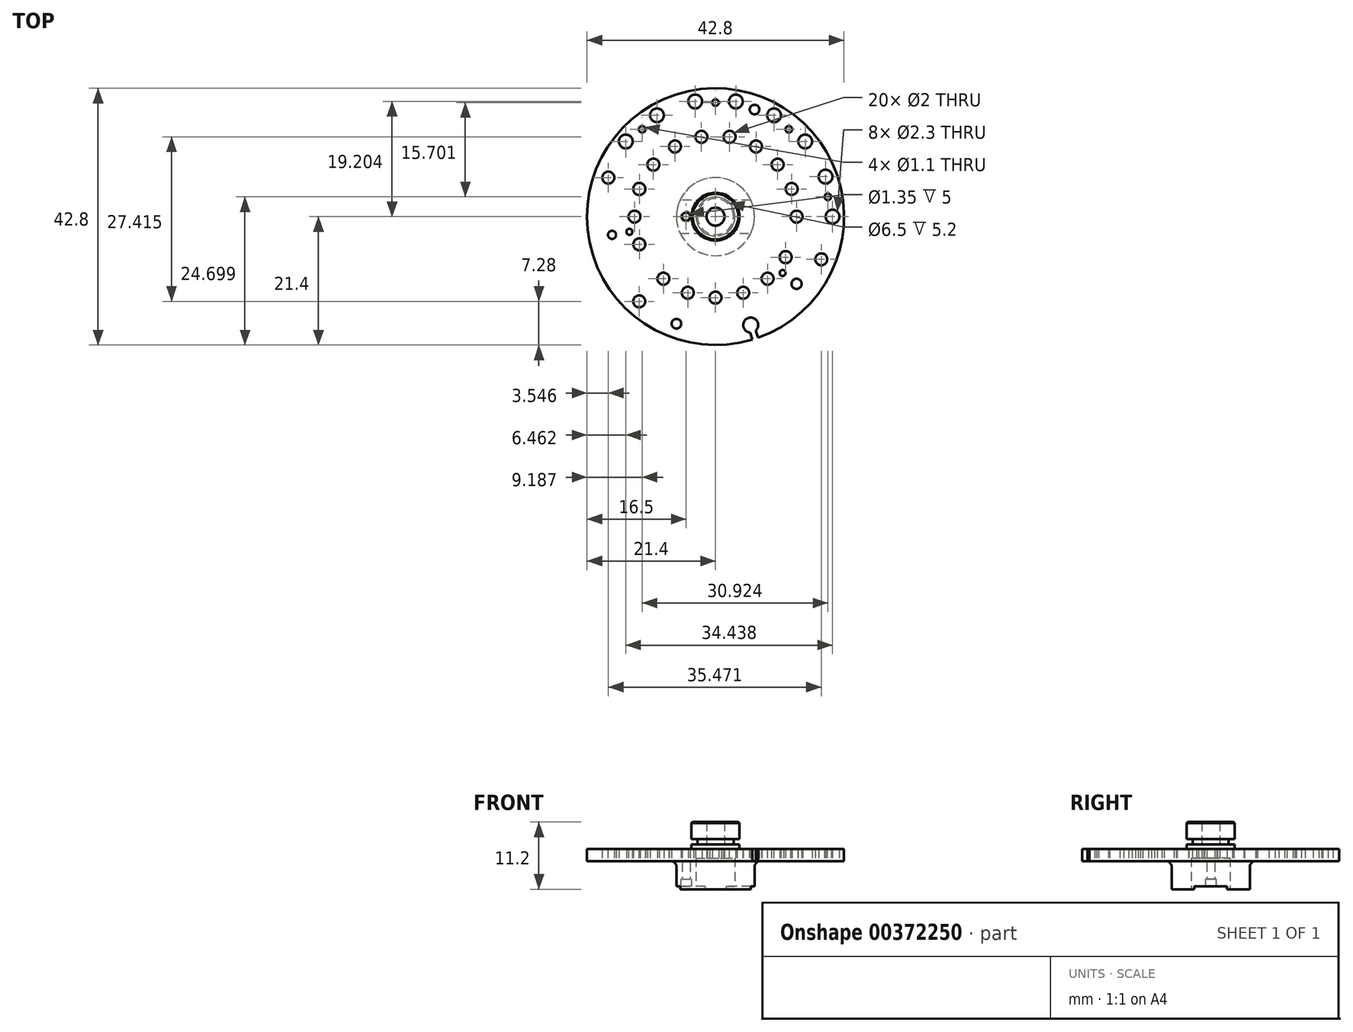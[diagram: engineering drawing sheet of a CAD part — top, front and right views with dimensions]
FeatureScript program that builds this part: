
annotation { "Feature Type Name" : "Feature", "Feature Type Description" : "" }
export const myFeature = defineFeature(function(context is Context, id is Id, definition is map)
    precondition{}
    {
        {
            var Q0;
            Q0=qCreatedBy(makeId("Front.planeOp"),FACE);
            var sketch = newSketch(context, id + "F0", { "sketchPlane" : qUnion([Q0])});
            skLineSegment(sketch, "E0", {"start": v(3.25, 0) * mm, "end": v(6.5, 0) * mm});
            skLineSegment(sketch, "E1", {"start": v(6.5, 0) * mm, "end": v(6.5, 4.7) * mm});
            skLineSegment(sketch, "E2", {"start": v(6.5, 4.7) * mm, "end": v(21.4, 4.7) * mm});
            skLineSegment(sketch, "E3", {"start": v(21.4, 4.7) * mm, "end": v(21.4, 6.7) * mm});
            skLineSegment(sketch, "E4", {"start": v(21.4, 6.7) * mm, "end": v(4, 6.7) * mm});
            skLineSegment(sketch, "E5", {"start": v(4, 6.7) * mm, "end": v(4, 7.5) * mm});
            skLineSegment(sketch, "E6", {"start": v(4, 11.2) * mm, "end": v(1.5, 11.2) * mm});
            skLineSegment(sketch, "E7", {"start": v(1.5, 11.2) * mm, "end": v(1.5, 5.2) * mm});
            skLineSegment(sketch, "E8", {"start": v(1.5, 5.2) * mm, "end": v(3.25, 5.2) * mm});
            skLineSegment(sketch, "E9", {"start": v(3.25, 5.2) * mm, "end": v(3.25, 0) * mm});
            skLineSegment(sketch, "E10", {"start": v(4, 7.5) * mm, "end": v(3, 7.5) * mm});
            skLineSegment(sketch, "E11", {"start": v(3, 7.5) * mm, "end": v(3, 8.35) * mm});
            skLineSegment(sketch, "E12", {"start": v(3, 8.35) * mm, "end": v(4, 8.35) * mm});
            skLineSegment(sketch, "E13", {"start": v(4, 8.35) * mm, "end": v(4, 11.2) * mm});
            skLineSegment(sketch, "E14", {"start": v(0, 0) * mm, "end": v(0, 11.2) * mm, "construction": true});
            skSolve(sketch);
        }
        {
            var Q0;
            Q0=makeQuery(id+"F0.imprint","IMPRINT",FACE,{"disambiguationData":[TD([[makeQuery(id+"F0.imprint","IMPRINT",EDGE,{"derivedFrom":sQuery(id+"F0.wireOp",EDGE,"E0")}),1.0]])]});
            var Q1;
            Q1=sQuery(id+"F0.wireOp",EDGE,"E14");
            revolve(context, id + "F1", {"entities" : qUnion([Q0]), "axis" : qUnion([Q1]), "revolveType" : RevolveType.FULL});
        }
        {
            var Q0;
            Q0=makeQuery(id+"F1.opRevolve","SWEPT_FACE",FACE,{"disambiguationData":[OSD([sQuery(id+"F0.wireOp",EDGE,"E2")])]});
            var sketch = newSketch(context, id + "F2", { "sketchPlane" : qUnion([Q0])});
            skLineSegment(sketch, "E15", {"start": v(21.4, 0) * mm, "end": v(0, 0) * mm, "construction": true});
            skLineSegment(sketch, "E16", {"start": v(0, 0) * mm, "end": v(20.1, -7.32) * mm, "construction": true});
            skLineSegment(sketch, "E17", {"start": v(0, 0) * mm, "end": v(16.4, -13.76) * mm, "construction": true});
            skLineSegment(sketch, "E18", {"start": v(0, 0) * mm, "end": v(10.7, -18.53) * mm, "construction": true});
            skLineSegment(sketch, "E19", {"start": v(0, 0) * mm, "end": v(3.72, -21.07) * mm, "construction": true});
            skLineSegment(sketch, "E20", {"start": v(0, 0) * mm, "end": v(-3.72, -21.07) * mm, "construction": true});
            skLineSegment(sketch, "E21", {"start": v(0, 0) * mm, "end": v(-10.7, -18.53) * mm, "construction": true});
            skLineSegment(sketch, "E22", {"start": v(0, 0) * mm, "end": v(-16.4, -13.76) * mm, "construction": true});
            skLineSegment(sketch, "E23", {"start": v(0, 0) * mm, "end": v(-20.1, -7.32) * mm, "construction": true});
            skLineSegment(sketch, "E24", {"start": v(0, 0) * mm, "end": v(-21.4, 0) * mm, "construction": true});
            skLineSegment(sketch, "E25", {"start": v(0, 0) * mm, "end": v(-20.1, 7.32) * mm, "construction": true});
            skLineSegment(sketch, "E26", {"start": v(0, 0) * mm, "end": v(18.53, 10.7) * mm, "construction": true});
            skLineSegment(sketch, "E27", {"start": v(0, 0) * mm, "end": v(13.76, 16.4) * mm, "construction": true});
            skLineSegment(sketch, "E28", {"start": v(0, 0) * mm, "end": v(7.32, 20.1) * mm, "construction": true});
            skLineSegment(sketch, "E29", {"start": v(0, 0) * mm, "end": v(0, 21.4) * mm, "construction": true});
            skLineSegment(sketch, "E30", {"start": v(0, 0) * mm, "end": v(-7.32, 20.1) * mm, "construction": true});
            skLineSegment(sketch, "E31", {"start": v(0, 0) * mm, "end": v(-13.76, 16.4) * mm, "construction": true});
            skCircle(sketch, "E32", {"center": v(0, 0) * mm, "radius": 19.5 * mm, "construction": true});
            skCircle(sketch, "E33", {"center": v(0, 0) * mm, "radius": 13.5 * mm, "construction": true});
            skCircle(sketch, "E34", {"center": v(19.5, 0) * mm, "radius": 1.15 * mm});
            skCircle(sketch, "E35", {"center": v(18.32, -6.67) * mm, "radius": 1.15 * mm});
            skCircle(sketch, "E36", {"center": v(14.94, -12.53) * mm, "radius": 1.15 * mm});
            skCircle(sketch, "E37", {"center": v(9.75, -16.89) * mm, "radius": 1.15 * mm});
            skCircle(sketch, "E38", {"center": v(3.39, -19.2) * mm, "radius": 1.15 * mm});
            skCircle(sketch, "E39", {"center": v(-3.39, -19.2) * mm, "radius": 1.15 * mm});
            skCircle(sketch, "E40", {"center": v(-9.75, -16.89) * mm, "radius": 1.15 * mm});
            skCircle(sketch, "E41", {"center": v(-14.94, -12.53) * mm, "radius": 1.15 * mm});
            skCircle(sketch, "E42", {"center": v(-17.85, -6.5) * mm, "radius": 1 * mm});
            skCircle(sketch, "E43", {"center": v(11.7, 6.75) * mm, "radius": 1 * mm});
            skCircle(sketch, "E44", {"center": v(8.68, 10.34) * mm, "radius": 1 * mm});
            skCircle(sketch, "E45", {"center": v(12.69, -4.62) * mm, "radius": 1 * mm});
            skCircle(sketch, "E46", {"center": v(13.5, 0) * mm, "radius": 1 * mm});
            skCircle(sketch, "E47", {"center": v(10.34, -8.68) * mm, "radius": 1 * mm});
            skCircle(sketch, "E48", {"center": v(6.75, -11.7) * mm, "radius": 1 * mm});
            skCircle(sketch, "E49", {"center": v(2.34, -13.3) * mm, "radius": 1 * mm});
            skCircle(sketch, "E50", {"center": v(-2.34, -13.3) * mm, "radius": 1 * mm});
            skCircle(sketch, "E51", {"center": v(-6.75, -11.7) * mm, "radius": 1 * mm});
            skCircle(sketch, "E52", {"center": v(-10.34, -8.68) * mm, "radius": 1 * mm});
            skCircle(sketch, "E53", {"center": v(-12.69, -4.62) * mm, "radius": 1 * mm});
            skCircle(sketch, "E54", {"center": v(-13.5, 0) * mm, "radius": 1 * mm});
            skCircle(sketch, "E55", {"center": v(-12.69, 4.62) * mm, "radius": 1 * mm});
            skCircle(sketch, "E56", {"center": v(-8.68, 10.34) * mm, "radius": 1 * mm});
            skCircle(sketch, "E57", {"center": v(-4.62, 12.69) * mm, "radius": 1 * mm});
            skCircle(sketch, "E58", {"center": v(0, 13.5) * mm, "radius": 1 * mm});
            skCircle(sketch, "E59", {"center": v(4.62, 12.69) * mm, "radius": 1 * mm});
            skLineSegment(sketch, "E60", {"start": v(0, 0) * mm, "end": v(21.07, -3.72) * mm, "construction": true});
            skLineSegment(sketch, "E61", {"start": v(0, 0) * mm, "end": v(13.76, -16.4) * mm, "construction": true});
            skLineSegment(sketch, "E62", {"start": v(0, 0) * mm, "end": v(7.32, -20.1) * mm, "construction": true});
            skLineSegment(sketch, "E63", {"start": v(0, 0) * mm, "end": v(0, -21.4) * mm, "construction": true});
            skLineSegment(sketch, "E64", {"start": v(0, 0) * mm, "end": v(-13.76, -16.4) * mm, "construction": true});
            skCircle(sketch, "E65", {"center": v(18.71, -3.3) * mm, "radius": 0.55 * mm});
            skCircle(sketch, "E66", {"center": v(12.21, -14.55) * mm, "radius": 0.55 * mm});
            skCircle(sketch, "E67", {"center": v(0, -19) * mm, "radius": 0.55 * mm});
            skCircle(sketch, "E68", {"center": v(-12.21, -14.55) * mm, "radius": 0.55 * mm});
            skCircle(sketch, "E69", {"center": v(6.5, -17.85) * mm, "radius": 0.8 * mm});
            skCircle(sketch, "E70", {"center": v(0, 0) * mm, "radius": 19 * mm, "construction": true});
            skLineSegment(sketch, "E71", {"start": v(0, 0) * mm, "end": v(17.62, 7.12) * mm, "construction": true});
            skCircle(sketch, "E72", {"center": v(17.62, 7.12) * mm, "radius": 1 * mm});
            skLineSegment(sketch, "E73", {"start": v(0, 0) * mm, "end": v(5.87, 18.07) * mm, "construction": true});
            skArc(sketch, "E74", {"start": v(5.75, 19.31) * mm, "mid": v(5.49, 16.88) * mm, "end": v(6.7, 19) * mm});
            skLineSegment(sketch, "E75", {"start": v(5.75, 19.31) * mm, "end": v(6.14, 20.5) * mm});
            skLineSegment(sketch, "E76", {"start": v(6.7, 19) * mm, "end": v(7.09, 20.2) * mm});
            skCircle(sketch, "E77", {"center": v(13.5, 11.2) * mm, "radius": 0.85 * mm});
            skCircle(sketch, "E78", {"center": v(11.18, 9.38) * mm, "radius": 0.5 * mm});
            skLineSegment(sketch, "E79", {"start": v(11.18, 9.38) * mm, "end": v(0, 0) * mm, "construction": true});
            skCircle(sketch, "E80", {"center": v(-6.5, 17.85) * mm, "radius": 0.8 * mm});
            skCircle(sketch, "E81", {"center": v(-12.71, 14.12) * mm, "radius": 1 * mm});
            skLineSegment(sketch, "E82", {"start": v(0, 0) * mm, "end": v(-12.71, 14.12) * mm, "construction": true});
            skLineSegment(sketch, "E83", {"start": v(0, 0) * mm, "end": v(-17.23, 3.04) * mm, "construction": true});
            skPoint(sketch, "E84", {"position": v(-14.33, 2.53) * mm});
            skCircle(sketch, "E85", {"center": v(-17.23, 3.04) * mm, "radius": 0.68 * mm});
            skCircle(sketch, "E86", {"center": v(-14.33, 2.53) * mm, "radius": 0.5 * mm});
            skSolve(sketch);
        }
        {
            var Q0;
            {Q0=qUnion([makeQuery(id+"F2.imprint","IMPRINT",FACE,{"disambiguationData":[TD([[makeQuery(id+"F2.imprint","IMPRINT",EDGE,{"derivedFrom":sQuery(id+"F2.wireOp",EDGE,"E34")}),1.0]])]}),makeQuery(id+"F2.imprint","IMPRINT",FACE,{"disambiguationData":[TD([[makeQuery(id+"F2.imprint","IMPRINT",EDGE,{"derivedFrom":sQuery(id+"F2.wireOp",EDGE,"E35")}),1.0]])]}),makeQuery(id+"F2.imprint","IMPRINT",FACE,{"disambiguationData":[TD([[makeQuery(id+"F2.imprint","IMPRINT",EDGE,{"derivedFrom":sQuery(id+"F2.wireOp",EDGE,"E36")}),1.0]])]}),makeQuery(id+"F2.imprint","IMPRINT",FACE,{"disambiguationData":[TD([[makeQuery(id+"F2.imprint","IMPRINT",EDGE,{"derivedFrom":sQuery(id+"F2.wireOp",EDGE,"E37")}),1.0]])]}),makeQuery(id+"F2.imprint","IMPRINT",FACE,{"disambiguationData":[TD([[makeQuery(id+"F2.imprint","IMPRINT",EDGE,{"derivedFrom":sQuery(id+"F2.wireOp",EDGE,"E38")}),1.0]])]}),makeQuery(id+"F2.imprint","IMPRINT",FACE,{"disambiguationData":[TD([[makeQuery(id+"F2.imprint","IMPRINT",EDGE,{"derivedFrom":sQuery(id+"F2.wireOp",EDGE,"E39")}),1.0]])]}),makeQuery(id+"F2.imprint","IMPRINT",FACE,{"disambiguationData":[TD([[makeQuery(id+"F2.imprint","IMPRINT",EDGE,{"derivedFrom":sQuery(id+"F2.wireOp",EDGE,"E40")}),1.0]])]}),makeQuery(id+"F2.imprint","IMPRINT",FACE,{"disambiguationData":[TD([[makeQuery(id+"F2.imprint","IMPRINT",EDGE,{"derivedFrom":sQuery(id+"F2.wireOp",EDGE,"E41")}),1.0]])]}),makeQuery(id+"F2.imprint","IMPRINT",FACE,{"disambiguationData":[TD([[makeQuery(id+"F2.imprint","IMPRINT",EDGE,{"derivedFrom":sQuery(id+"F2.wireOp",EDGE,"E42")}),1.0]])]}),makeQuery(id+"F2.imprint","IMPRINT",FACE,{"disambiguationData":[TD([[makeQuery(id+"F2.imprint","IMPRINT",EDGE,{"derivedFrom":sQuery(id+"F2.wireOp",EDGE,"E43")}),1.0]])]}),makeQuery(id+"F2.imprint","IMPRINT",FACE,{"disambiguationData":[TD([[makeQuery(id+"F2.imprint","IMPRINT",EDGE,{"derivedFrom":sQuery(id+"F2.wireOp",EDGE,"E44")}),1.0]])]}),makeQuery(id+"F2.imprint","IMPRINT",FACE,{"disambiguationData":[TD([[makeQuery(id+"F2.imprint","IMPRINT",EDGE,{"derivedFrom":sQuery(id+"F2.wireOp",EDGE,"E45")}),1.0]])]}),makeQuery(id+"F2.imprint","IMPRINT",FACE,{"disambiguationData":[TD([[makeQuery(id+"F2.imprint","IMPRINT",EDGE,{"derivedFrom":sQuery(id+"F2.wireOp",EDGE,"E46")}),1.0]])]}),makeQuery(id+"F2.imprint","IMPRINT",FACE,{"disambiguationData":[TD([[makeQuery(id+"F2.imprint","IMPRINT",EDGE,{"derivedFrom":sQuery(id+"F2.wireOp",EDGE,"E47")}),1.0]])]}),makeQuery(id+"F2.imprint","IMPRINT",FACE,{"disambiguationData":[TD([[makeQuery(id+"F2.imprint","IMPRINT",EDGE,{"derivedFrom":sQuery(id+"F2.wireOp",EDGE,"E48")}),1.0]])]}),makeQuery(id+"F2.imprint","IMPRINT",FACE,{"disambiguationData":[TD([[makeQuery(id+"F2.imprint","IMPRINT",EDGE,{"derivedFrom":sQuery(id+"F2.wireOp",EDGE,"E49")}),1.0]])]}),makeQuery(id+"F2.imprint","IMPRINT",FACE,{"disambiguationData":[TD([[makeQuery(id+"F2.imprint","IMPRINT",EDGE,{"derivedFrom":sQuery(id+"F2.wireOp",EDGE,"E50")}),1.0]])]}),makeQuery(id+"F2.imprint","IMPRINT",FACE,{"disambiguationData":[TD([[makeQuery(id+"F2.imprint","IMPRINT",EDGE,{"derivedFrom":sQuery(id+"F2.wireOp",EDGE,"E51")}),1.0]])]}),makeQuery(id+"F2.imprint","IMPRINT",FACE,{"disambiguationData":[TD([[makeQuery(id+"F2.imprint","IMPRINT",EDGE,{"derivedFrom":sQuery(id+"F2.wireOp",EDGE,"E52")}),1.0]])]}),makeQuery(id+"F2.imprint","IMPRINT",FACE,{"disambiguationData":[TD([[makeQuery(id+"F2.imprint","IMPRINT",EDGE,{"derivedFrom":sQuery(id+"F2.wireOp",EDGE,"E53")}),1.0]])]}),makeQuery(id+"F2.imprint","IMPRINT",FACE,{"disambiguationData":[TD([[makeQuery(id+"F2.imprint","IMPRINT",EDGE,{"derivedFrom":sQuery(id+"F2.wireOp",EDGE,"E54")}),1.0]])]}),makeQuery(id+"F2.imprint","IMPRINT",FACE,{"disambiguationData":[TD([[makeQuery(id+"F2.imprint","IMPRINT",EDGE,{"derivedFrom":sQuery(id+"F2.wireOp",EDGE,"E55")}),1.0]])]}),makeQuery(id+"F2.imprint","IMPRINT",FACE,{"disambiguationData":[TD([[makeQuery(id+"F2.imprint","IMPRINT",EDGE,{"derivedFrom":sQuery(id+"F2.wireOp",EDGE,"E56")}),1.0]])]}),makeQuery(id+"F2.imprint","IMPRINT",FACE,{"disambiguationData":[TD([[makeQuery(id+"F2.imprint","IMPRINT",EDGE,{"derivedFrom":sQuery(id+"F2.wireOp",EDGE,"E57")}),1.0]])]}),makeQuery(id+"F2.imprint","IMPRINT",FACE,{"disambiguationData":[TD([[makeQuery(id+"F2.imprint","IMPRINT",EDGE,{"derivedFrom":sQuery(id+"F2.wireOp",EDGE,"E58")}),1.0]])]}),makeQuery(id+"F2.imprint","IMPRINT",FACE,{"disambiguationData":[TD([[makeQuery(id+"F2.imprint","IMPRINT",EDGE,{"derivedFrom":sQuery(id+"F2.wireOp",EDGE,"E59")}),1.0]])]}),makeQuery(id+"F2.imprint","IMPRINT",FACE,{"disambiguationData":[TD([[makeQuery(id+"F2.imprint","IMPRINT",EDGE,{"derivedFrom":sQuery(id+"F2.wireOp",EDGE,"E65")}),1.0]])]}),makeQuery(id+"F2.imprint","IMPRINT",FACE,{"disambiguationData":[TD([[makeQuery(id+"F2.imprint","IMPRINT",EDGE,{"derivedFrom":sQuery(id+"F2.wireOp",EDGE,"E66")}),1.0]])]}),makeQuery(id+"F2.imprint","IMPRINT",FACE,{"disambiguationData":[TD([[makeQuery(id+"F2.imprint","IMPRINT",EDGE,{"derivedFrom":sQuery(id+"F2.wireOp",EDGE,"E67")}),1.0]])]}),makeQuery(id+"F2.imprint","IMPRINT",FACE,{"disambiguationData":[TD([[makeQuery(id+"F2.imprint","IMPRINT",EDGE,{"derivedFrom":sQuery(id+"F2.wireOp",EDGE,"E68")}),1.0]])]}),makeQuery(id+"F2.imprint","IMPRINT",FACE,{"disambiguationData":[TD([[makeQuery(id+"F2.imprint","IMPRINT",EDGE,{"derivedFrom":sQuery(id+"F2.wireOp",EDGE,"E69")}),1.0]])]}),makeQuery(id+"F2.imprint","IMPRINT",FACE,{"disambiguationData":[TD([[makeQuery(id+"F2.imprint","IMPRINT",EDGE,{"derivedFrom":sQuery(id+"F2.wireOp",EDGE,"E72")}),1.0]])]}),makeQuery(id+"F2.imprint","IMPRINT",FACE,{"disambiguationData":[TD([[makeQuery(id+"F2.imprint","IMPRINT",EDGE,{"derivedFrom":sQuery(id+"F2.wireOp",EDGE,"E77")}),1.0]])]}),makeQuery(id+"F2.imprint","IMPRINT",FACE,{"disambiguationData":[TD([[makeQuery(id+"F2.imprint","IMPRINT",EDGE,{"derivedFrom":sQuery(id+"F2.wireOp",EDGE,"E78")}),1.0]])]}),makeQuery(id+"F2.imprint","IMPRINT",FACE,{"disambiguationData":[TD([[makeQuery(id+"F2.imprint","IMPRINT",EDGE,{"derivedFrom":sQuery(id+"F2.wireOp",EDGE,"E80")}),1.0]])]}),makeQuery(id+"F2.imprint","IMPRINT",FACE,{"disambiguationData":[TD([[makeQuery(id+"F2.imprint","IMPRINT",EDGE,{"derivedFrom":sQuery(id+"F2.wireOp",EDGE,"E81")}),1.0]])]}),makeQuery(id+"F2.imprint","IMPRINT",FACE,{"disambiguationData":[TD([[makeQuery(id+"F2.imprint","IMPRINT",EDGE,{"derivedFrom":sQuery(id+"F2.wireOp",EDGE,"E85")}),1.0]])]}),makeQuery(id+"F2.imprint","IMPRINT",FACE,{"disambiguationData":[TD([[makeQuery(id+"F2.imprint","IMPRINT",EDGE,{"derivedFrom":sQuery(id+"F2.wireOp",EDGE,"E86")}),1.0]])]})]);}
            var Q1;
            Q1=makeQuery(id+"F2.imprint","IMPRINT",FACE,{"disambiguationData":[TD([[makeQuery(id+"F2.imprint","IMPRINT",EDGE,{"derivedFrom":sQuery(id+"F2.wireOp",EDGE,"E74")}),1.0]])]});
            extrude(context, id + "F3", {"entities" : qUnion([Q0, Q1]), "operationType" : NewBodyOperationType.REMOVE, "endBound" : BoundingType.THROUGH_ALL, "oppositeDirection" : true, "depth" : 25 * mm});
        }
        {
            var Q0;
            Q0=makeQuery(id+"F1.opRevolve","SWEPT_EDGE",EDGE,{"disambiguationData":[OSD([sQuery(id+"F0.wireOp",EDGE,"E1"),sQuery(id+"F0.wireOp",EDGE,"E2")])]});
            fillet(context, id + "F4", {"entities" : qUnion([Q0]), "radius" : 1 * mm, "tangentPropagation" : true, "allowEdgeOverflow" : false});
        }
        {
            var Q0;
            Q0=makeQuery(id+"F1.opRevolve","SWEPT_EDGE",EDGE,{"disambiguationData":[OSD([sQuery(id+"F0.wireOp",EDGE,"E4"),sQuery(id+"F0.wireOp",EDGE,"E5")])]});
            fillet(context, id + "F5", {"entities" : qUnion([Q0]), "radius" : 0.2 * mm, "tangentPropagation" : true, "allowEdgeOverflow" : false});
        }
        {
            var Q0;
            Q0=makeQuery(id+"F1.opRevolve","SWEPT_EDGE",EDGE,{"disambiguationData":[OSD([sQuery(id+"F0.wireOp",EDGE,"E6"),sQuery(id+"F0.wireOp",EDGE,"E13")])]});
            chamfer(context, id + "F6", {"entities" : qUnion([Q0]), "width" : 0.2 * mm, "tangentPropagation" : true});
        }
        {
            var Q0;
            Q0=makeQuery(id+"F1.opRevolve","SWEPT_FACE",FACE,{"disambiguationData":[OSD([sQuery(id+"F0.wireOp",EDGE,"E0")])]});
            var sketch = newSketch(context, id + "F7", { "sketchPlane" : qUnion([Q0])});
            skLineSegment(sketch, "E87", {"start": v(5.89, -2.75) * mm, "end": v(-5.89, -2.75) * mm});
            skLineSegment(sketch, "E88", {"start": v(-5.89, 2.75) * mm, "end": v(5.89, 2.75) * mm});
            skSolve(sketch);
        }
        {
            var Q0;
            {var subQ0=sQuery(id+"F0.wireOp",EDGE,"E0");var subQ4=sQuery(id+"F7.wireOp",EDGE,"E87");var subQ6=makeQuery(id+"F1.opRevolve","SWEPT_EDGE",EDGE,{"disambiguationData":[OSD([subQ0,sQuery(id+"F0.wireOp",EDGE,"E1")])]});var subQ8=makeQuery(id+"F7.imprint","INTERSECT",VERTEX,{"disambiguationData":[OD(0.0)],"derivedFrom":[subQ6,subQ4]});Q0=makeQuery(id+"F7.imprint","IMPRINT",FACE,{"disambiguationData":[TD([[makeQuery(id+"F7.imprint","IMPRINT",EDGE,{"disambiguationData":[TD([[subQ8,-1.0]])],"derivedFrom":subQ4}),-1.0]])]});}
            var Q1;
            {var subQ0=sQuery(id+"F0.wireOp",EDGE,"E0");var subQ4=sQuery(id+"F7.wireOp",EDGE,"E87");var subQ6=makeQuery(id+"F1.opRevolve","SWEPT_EDGE",EDGE,{"disambiguationData":[OSD([subQ0,sQuery(id+"F0.wireOp",EDGE,"E1")])]});var subQ8=makeQuery(id+"F7.imprint","INTERSECT",VERTEX,{"disambiguationData":[OD(1.0)],"derivedFrom":[subQ6,subQ4]});Q1=makeQuery(id+"F7.imprint","IMPRINT",FACE,{"disambiguationData":[TD([[makeQuery(id+"F7.imprint","IMPRINT",EDGE,{"disambiguationData":[TD([[subQ8,1.0]])],"derivedFrom":subQ4}),-1.0]])]});}
            extrude(context, id + "F8", {"entities" : qUnion([Q0, Q1]), "operationType" : NewBodyOperationType.REMOVE, "oppositeDirection" : true, "depth" : 0.5 * mm});
        }
        {
            var Q0;
            {var subQ0=sQuery(id+"F0.wireOp",EDGE,"E0");var subQ1=sQuery(id+"F0.wireOp",EDGE,"E1");var subQ2=sQuery(id+"F0.wireOp",EDGE,"E9");var subQ3=sQuery(id+"F7.wireOp",EDGE,"E87");var subQ4=sQuery(id+"F7.wireOp",EDGE,"E88");var subQ5=makeQuery(id+"F1.opRevolve","SWEPT_EDGE",EDGE,{"disambiguationData":[OSD([subQ0,subQ2])]});var subQ6=makeQuery(id+"F7.imprint","INTERSECT",VERTEX,{"disambiguationData":[OD(1.0)],"derivedFrom":[subQ5,subQ3]});var subQ7=makeQuery(id+"F1.opRevolve","SWEPT_EDGE",EDGE,{"disambiguationData":[OSD([subQ0,subQ1])]});var subQ8=makeQuery(id+"F7.imprint","INTERSECT",VERTEX,{"disambiguationData":[OD(1.0)],"derivedFrom":[subQ7,subQ3]});var subQ10=makeQuery(id+"F7.imprint","INTERSECT",VERTEX,{"disambiguationData":[OD(0.0)],"derivedFrom":[subQ7,subQ4]});Q0=makeQuery(id+"F8.boolean.opBoolean","COPY",FACE,{"derivedFrom":makeQuery(id+"F8.opExtrude","CAP_FACE",FACE,{"disambiguationData":[OSD([subQ0,subQ1,subQ2,subQ3,subQ4]),TDD([makeQuery(id+"F7.imprint","IMPRINT",EDGE,{"disambiguationData":[TD([[subQ8,1.0]])],"derivedFrom":subQ3}),makeQuery(id+"F7.imprint","IMPRINT",EDGE,{"disambiguationData":[TD([[subQ10,-1.0]])],"derivedFrom":subQ4}),makeQuery(id+"F7.imprint","IMPRINT",EDGE,{"disambiguationData":[TD([[subQ8,1.0]])],"derivedFrom":subQ7}),makeQuery(id+"F7.imprint","IMPRINT",EDGE,{"disambiguationData":[TD([[subQ6,1.0]])],"derivedFrom":subQ5})])],"isStart":false})});}
            var sketch = newSketch(context, id + "F9", { "sketchPlane" : qUnion([Q0])});
            skCircle(sketch, "E89", {"center": v(-4.9, 0) * mm, "radius": 0.68 * mm});
            skSolve(sketch);
        }
        {
            var Q0;
            Q0=makeQuery(id+"F9.imprint","IMPRINT",FACE,{"disambiguationData":[TD([[makeQuery(id+"F9.imprint","IMPRINT",EDGE,{"derivedFrom":sQuery(id+"F9.wireOp",EDGE,"E89")}),1.0]])]});
            extrude(context, id + "F10", {"entities" : qUnion([Q0]), "operationType" : NewBodyOperationType.REMOVE, "endBound" : BoundingType.THROUGH_ALL, "oppositeDirection" : true, "depth" : 25 * mm});
        }
        {
            var Q0;
            {var subQ0=sQuery(id+"F0.wireOp",EDGE,"E0");var subQ1=sQuery(id+"F0.wireOp",EDGE,"E1");var subQ2=sQuery(id+"F0.wireOp",EDGE,"E9");var subQ3=sQuery(id+"F7.wireOp",EDGE,"E87");var subQ4=sQuery(id+"F7.wireOp",EDGE,"E88");var subQ5=makeQuery(id+"F1.opRevolve","SWEPT_EDGE",EDGE,{"disambiguationData":[OSD([subQ0,subQ2])]});var subQ6=makeQuery(id+"F7.imprint","INTERSECT",VERTEX,{"disambiguationData":[OD(1.0)],"derivedFrom":[subQ5,subQ3]});var subQ7=makeQuery(id+"F1.opRevolve","SWEPT_EDGE",EDGE,{"disambiguationData":[OSD([subQ0,subQ1])]});var subQ8=makeQuery(id+"F7.imprint","INTERSECT",VERTEX,{"disambiguationData":[OD(1.0)],"derivedFrom":[subQ7,subQ3]});var subQ10=makeQuery(id+"F7.imprint","INTERSECT",VERTEX,{"disambiguationData":[OD(0.0)],"derivedFrom":[subQ7,subQ4]});Q0=makeQuery(id+"F8.boolean.opBoolean","COPY",FACE,{"derivedFrom":makeQuery(id+"F8.opExtrude","CAP_FACE",FACE,{"disambiguationData":[OSD([subQ0,subQ1,subQ2,subQ3,subQ4]),TDD([makeQuery(id+"F7.imprint","IMPRINT",EDGE,{"disambiguationData":[TD([[subQ8,1.0]])],"derivedFrom":subQ3}),makeQuery(id+"F7.imprint","IMPRINT",EDGE,{"disambiguationData":[TD([[subQ10,-1.0]])],"derivedFrom":subQ4}),makeQuery(id+"F7.imprint","IMPRINT",EDGE,{"disambiguationData":[TD([[subQ8,1.0]])],"derivedFrom":subQ7}),makeQuery(id+"F7.imprint","IMPRINT",EDGE,{"disambiguationData":[TD([[subQ6,1.0]])],"derivedFrom":subQ5})])],"isStart":false})});}
            var sketch = newSketch(context, id + "F11", { "sketchPlane" : qUnion([Q0])});
            skCircle(sketch, "E90", {"center": v(-4.9, 0) * mm, "radius": 0.9 * mm});
            skSolve(sketch);
        }
        {
            var Q0;
            {var subQ0=makeQuery(id+"F11.imprint","IMPRINT",EDGE,{"derivedFrom":makeQuery(id+"F10.boolean.opBoolean","COPY",EDGE,{"derivedFrom":makeQuery(id+"F10.opExtrude","CAP_EDGE",EDGE,{"disambiguationData":[OSD([sQuery(id+"F9.wireOp",EDGE,"E89")])],"isStart":true})})});Q0=qUnion([makeQuery(id+"F11.imprint","IMPRINT",FACE,{"disambiguationData":[TD([[subQ0,1.0]])]}),makeQuery(id+"F11.imprint","IMPRINT",FACE,{"disambiguationData":[TD([[makeQuery(id+"F11.imprint","IMPRINT",EDGE,{"derivedFrom":sQuery(id+"F11.wireOp",EDGE,"E90")}),1.0]])]})]);}
            extrude(context, id + "F12", {"entities" : qUnion([Q0]), "operationType" : NewBodyOperationType.REMOVE, "oppositeDirection" : true, "depth" : 1.2 * mm});
        }
    });
